# Revit family: KS ALU-PU 80, DS 20, m.Blz, M10-M12, Ø 42-168,3
name_source: partatom
category: HLS-Bauteile
units: mm (PartAtom-declared; Revit-internal decimal feet)

## family parameters
Arbeitsebenenbasiert = Ja
Beim Laden mit Abzugskörper schneiden = Nein
Bemaßung runder Anschluss = Durchmesser verwenden
Beschriftungsausrichtung beibehalten = Nein
Gemeinsam genutzt = Ja
Immer vertikal = Nein
Raumberechnungspunkt = Nein
Teiletyp = Normal

## types (15) — shared parameters
A = 46 mm  [stored 0.150919 ft]
Anschluss = M10/M12
Baustoffklasse = B2
DS = 20 mm  [stored 0.0656168 ft]
DVS = 18 mm  [stored 0.0590551 ft]
Dichte Kern = 80 kg/m³
Dichte Mantel = 2700 kg/m³
Dicke Mantel = 0.08 mm
Druckverteilung = Blechzylinder
Dämmkörper = ALU/PU
Dämmstärke = 20 mm  [stored 0.0656168 ft]
Fabrikat = MEFA
Firma = MEFA Befestigungs- und Montagesysteme GmbH
HGA = 22 mm  [stored 0.0721785 ft]
Kurztext1 = Kälteschelle RG80 ALU/PU
L = 100 mm
MB = 35 mm  [stored 0.114829 ft]
MD = 4 mm  [stored 0.0131234 ft]
Material = Stahl
Material Mantel = Alufolie
Materialname = S235
Mengeneinheit = St
Oberflaeche = galvanisch verzinkt
Rohrschellentyp = Maxima PSM
Schalenlänge = 100 mm
Vorgabe-Ansicht = 1219 mm
Wasserdampfdiffusionswiderstand = 18750 µ
Wärmeleitfähigkeit = 0.025 W/mK
max. Temperaturbeständigkeit = 120 °C
mittl. Nenndruckfestigkeit Kern = 0.5 N/mm²
stat. Belastung Kern = 0.1 N/mm²
vpe = 1

## per-type parameters (varying)
| type | AB | Anschlußhöhe | Artikelnummer | B | Breite | D | D0 | DF1 | DF2 | Dmax | Dmin | EAN | Gewicht | Gewicht pro Bauteil | H | Kurztext2 | R | RM | Rohraußendurchmesser Kupfer | Rohraußendurchmesser Stahl | S | max. zul. Last |
| Kälteschelle ALU-PU 80, DS 20, m.Blz, M10/M12, Ø 42,4 | 2 mm  [stored 0.00656168 ft] | 46 mm | 7560426/B | 152 mm | 151 mm | 42 mm | 82 mm | 31 mm  [stored 0.101706 ft] | 30 mm  [stored 0.0984252 ft] | 43 mm  [stored 0.141076 ft] | 40 mm  [stored 0.131234 ft] | 4250928443434 | 0.56 kg | 0.56 kg | 112 mm | 42,4 mm Iso 20 x 100 mm M10/M12 | 41 mm | 45 mm | 42 mm | 42,4 mm | 121 mm | 0.60 kN |
| Kälteschelle ALU-PU 80, DS 20, m.Blz, M10/M12, Ø 48,3 | 1 mm  [stored 0.00328084 ft] | 44 mm | 7560486/B | 152 mm | 151 mm | 48 mm | 88 mm | 27 mm  [stored 0.0885827 ft] | 27 mm  [stored 0.0885827 ft] | 50 mm  [stored 0.164042 ft] | 47 mm  [stored 0.154199 ft] | 4250928443458 | 0.57 kg | 0.57 kg | 118 mm | 48,3 mm Iso 20 x 100 mm M10/M12 | 44 mm | 48 mm |  | 48,3 mm | 125 mm | 0.70 kN |
| Kälteschelle ALU-PU 80, DS 20, m.Blz, M10/M12, Ø 54 | 2 mm  [stored 0.00656168 ft] | 46 mm | 7560543/B | 164 mm | 162 mm | 54 mm  [stored 0.177165 ft] | 94 mm | 29 mm  [stored 0.0951444 ft] | 29 mm  [stored 0.0951444 ft] | 58 mm  [stored 0.190289 ft] | 52 mm | 4250928443465 | 0.61 kg | 0.61 kg | 124 mm | 54 mm Iso 20 x 100 mm M10/M12 | 47 mm  [stored 0.154199 ft] | 51 mm  [stored 0.167323 ft] | 54 mm |  | 135 mm | 0.70 kN |
| Kälteschelle ALU-PU 80, DS 20, m.Blz, M10/M12, Ø 57 | 1 mm  [stored 0.00328084 ft] | 45 mm | 75605742/B | 164 mm | 162 mm | 57 mm  [stored 0.187008 ft] | 97 mm | 28 mm  [stored 0.0918635 ft] | 28 mm  [stored 0.0918635 ft] | 60 mm  [stored 0.19685 ft] | 56 mm  [stored 0.183727 ft] | 4250928443496 | 0.62 kg | 0.62 kg | 127 mm | 57 mm Iso 20 x 100 mm M10/M12 | 49 mm | 53 mm |  | 57 mm | 136 mm | 0.80 kN |
| Kälteschelle ALU-PU 80, DS 20, m.Blz, M10/M12, Ø 60,3 | 2 mm  [stored 0.00656168 ft] | 44 mm | 7560606/B | 164 mm | 162 mm | 60 mm  [stored 0.19685 ft] | 100 mm | 27 mm  [stored 0.0885827 ft] | 27 mm  [stored 0.0885827 ft] | 62 mm  [stored 0.203412 ft] | 58 mm  [stored 0.190289 ft] | 4250928443519 | 0.62 kg | 0.62 kg | 130 mm | 60,3 mm Iso 20 x 100 mm M10/M12 | 50 mm  [stored 0.164042 ft] | 54 mm  [stored 0.177165 ft] |  | 60,3 mm | 137 mm | 0.90 kN |
| Kälteschelle ALU-PU 80, DS 20, m.Blz, M10/M12, Ø 63,5 | 2 mm  [stored 0.00656168 ft] | 46 mm | 75606442/B | 174 mm | 172 mm | 64 mm | 104 mm | 30 mm  [stored 0.0984252 ft] | 30 mm  [stored 0.0984252 ft] | 66 mm | 62 mm  [stored 0.203412 ft] | 4250928443533 | 0.66 kg | 0.66 kg | 134 mm | 63,5 mm Iso 20 x 100 mm M10/M12 | 52 mm | 56 mm  [stored 0.183727 ft] |  | 63,5 mm | 144 mm | 0.90 kN |
| Kälteschelle ALU-PU 80, DS 20, m.Blz, M10/M12, Ø 70 | 2 mm  [stored 0.00656168 ft] | 44 mm | 75607042/B | 174 mm | 172 mm | 70 mm | 110 mm | 27 mm  [stored 0.0885827 ft] | 27 mm  [stored 0.0885827 ft] | 72 mm | 68 mm | 4250928443557 | 0.66 kg | 0.66 kg | 140 mm | 70 mm Iso 20 x 100 mm M10/M12 | 55 mm  [stored 0.180446 ft] | 59 mm |  | 70 mm | 147 mm | 1.00 kN |
| Kälteschelle ALU-PU 80, DS 20, m.Blz, M10/M12, Ø 76,1 | 2 mm  [stored 0.00656168 ft] | 47 mm | 75607642/B | 186 mm | 184 mm | 76 mm | 116 mm | 29 mm  [stored 0.0951444 ft] | 29 mm  [stored 0.0951444 ft] | 80 mm | 74 mm | 4250928443564 | 0.71 kg | 0.71 kg | 146 mm | 76,1 mm Iso 20 x 100 mm M10/M12 | 58 mm  [stored 0.190289 ft] | 62 mm  [stored 0.203412 ft] |  | 76,1 mm | 157 mm | 1.10 kN |
| Kälteschelle ALU-PU 80, DS 20, m.Blz, M10/M12, Ø 88,9 | 3 mm  [stored 0.00984252 ft] | 47 mm | 7560896/B | 210 mm | 209 mm | 89 mm | 129 mm | 35 mm  [stored 0.114829 ft] | 35 mm  [stored 0.114829 ft] | 92 mm | 86 mm | 4250928443595 | 0.98 kg | 0.98 kg | 159 mm | 88,9 mm Iso 20 x 100 mm M10/M12 | 64 mm | 68 mm |  | 88,9 mm | 175 mm | 1.30 kN |
| Kälteschelle ALU-PU 80, DS 20, m.Blz, M10/M12, Ø108 | 2 mm  [stored 0.00656168 ft] | 46 mm | 75610844/B | 227 mm | 226 mm | 108 mm | 148 mm | 34 mm | 35 mm  [stored 0.114829 ft] | 110 mm | 106 mm | 4250928443618 | 1.07 kg | 1.07 kg | 178 mm | 108 mm Iso 20 x 100 mm M10/M12 | 74 mm | 78 mm |  | 108 mm | 193 mm | 1.60 kN |
| Kälteschelle ALU-PU 80, DS 20, m.Blz, M10/M12, Ø114,3 | 2 mm  [stored 0.00656168 ft] | 47 mm | 75611444/B | 235 mm | 234 mm | 114 mm | 154 mm | 35 mm  [stored 0.114829 ft] | 36 mm  [stored 0.11811 ft] | 116 mm | 112 mm | 4250928443632 | 1.12 kg | 1.12 kg | 184 mm | 114,3 mm Iso 20 x 100 mm M10/M12 | 77 mm | 81 mm |  | 114.3 mm | 200 mm | 1.70 kN |
| Kälteschelle ALU-PU 80, DS 20, m.Blz, M10/M12, Ø133 | 1 mm  [stored 0.00328084 ft] | 47 mm | 75613344/B | 253 mm | 252 mm | 133 mm | 173 mm | 35 mm  [stored 0.114829 ft] | 35 mm  [stored 0.114829 ft] | 135 mm | 132 mm | 4250928443656 | 1.22 kg | 1.22 kg | 203 mm | 133 mm Iso 20 x 100 mm M10/M12 | 87 mm | 91 mm |  | 133 mm | 218 mm | 1.90 kN |
| Kälteschelle ALU-PU 80, DS 20, m.Blz, M10/M12, Ø139,7 | 2 mm  [stored 0.00656168 ft] | 45 mm | 75614044/B | 253 mm | 252 mm | 140 mm | 180 mm | 32 mm  [stored 0.104987 ft] | 33 mm  [stored 0.108268 ft] | 140 mm | 138 mm | 4250928443717 | 1.22 kg | 1.22 kg | 210 mm | 139,7 mm Iso 20 x 100 mm M10/M12 | 90 mm | 94 mm |  | 139,7 mm | 221 mm | 2.00 kN |
| Kälteschelle ALU-PU 80, DS 20, m.Blz, M10/M12, Ø159 | 1 mm  [stored 0.00328084 ft] | 47 mm | 75615944/B | 277 mm | 278 mm | 159 mm | 199 mm | 32 mm  [stored 0.104987 ft] | 33 mm  [stored 0.108268 ft] | 164 mm | 158 mm | 4250928443755 | 1.37 kg | 1.37 kg | 229 mm | 159 mm Iso 20 x 100 mm M10/M12 | 100 mm | 104 mm |  | 159 mm | 245 mm | 2.30 kN |
| Kälteschelle ALU-PU 80, DS 20, m.Blz, M10/M12, Ø168,3 | 1 mm  [stored 0.00328084 ft] | 46 mm | 75616844/B | 288 mm | 287 mm | 168 mm | 208 mm | 34 mm | 34 mm | 172 mm | 167 mm | 4250928443793 | 1.41 kg | 1.41 kg | 238 mm | 168,3 mm Iso 20 x 100 mm M10/M12 | 104 mm | 108 mm |  | 168,3 mm | 254 mm | 2.50 kN |

note: [stored X ft] marks values corroborated as IEEE doubles in the binary element streams (Revit-internal decimal feet)

## geometry (parser evidence)
native form markers: Sweep x4
no freeform markers — native parametric forms only
